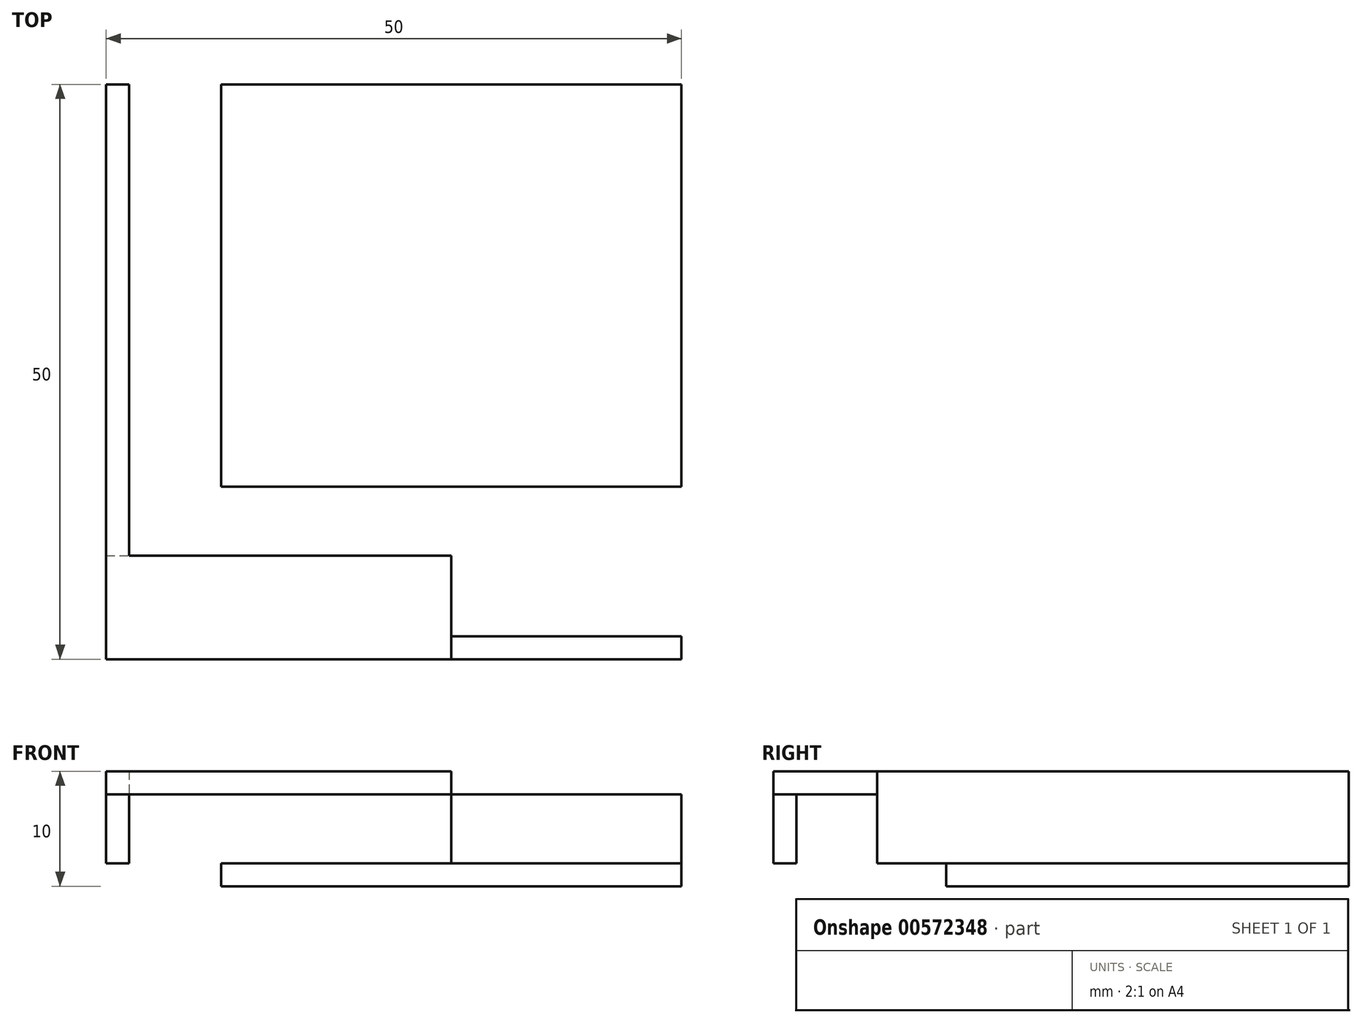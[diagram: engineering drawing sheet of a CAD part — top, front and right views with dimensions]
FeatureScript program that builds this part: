
annotation { "Feature Type Name" : "Feature", "Feature Type Description" : "" }
export const myFeature = defineFeature(function(context is Context, id is Id, definition is map)
    precondition{}
    {
        {
            var Q0;
            Q0=qCreatedBy(makeId("Top.planeOp"),FACE);
            var sketch = newSketch(context, id + "F0", { "sketchPlane" : qUnion([Q0])});
            skLineSegment(sketch, "E0.bottom", {"start": v(-25, 25) * mm, "end": v(25, 25) * mm});
            skLineSegment(sketch, "E0.top", {"start": v(-25, -25) * mm, "end": v(25, -25) * mm});
            skLineSegment(sketch, "E0.left", {"start": v(-25, 25) * mm, "end": v(-25, -25) * mm});
            skLineSegment(sketch, "E0.right", {"start": v(25, 25) * mm, "end": v(25, -25) * mm});
            skPoint(sketch, "E0.middle", {"position": v(0, 0) * mm});
            skLineSegment(sketch, "E1.bottom", {"start": v(-25, -25) * mm, "end": v(5, -25) * mm});
            skLineSegment(sketch, "E1.top", {"start": v(-25, -16) * mm, "end": v(5, -16) * mm});
            skLineSegment(sketch, "E1.left", {"start": v(-25, -25) * mm, "end": v(-25, -16) * mm});
            skLineSegment(sketch, "E1.right", {"start": v(5, -25) * mm, "end": v(5, -16) * mm});
            skLineSegment(sketch, "E2.bottom", {"start": v(25, 25) * mm, "end": v(-15, 25) * mm});
            skLineSegment(sketch, "E2.top", {"start": v(25, -10) * mm, "end": v(-15, -10) * mm});
            skLineSegment(sketch, "E2.left", {"start": v(25, 25) * mm, "end": v(25, -10) * mm});
            skLineSegment(sketch, "E2.right", {"start": v(-15, 25) * mm, "end": v(-15, -10) * mm});
            skSolve(sketch);
        }
        {
            var Q0;
            Q0=makeQuery(id+"F0.imprint","IMPRINT",FACE,{"disambiguationData":[TD([[makeQuery(id+"F0.imprint","IMPRINT",EDGE,{"derivedFrom":sQuery(id+"F0.wireOp",EDGE,"E0.bottom")}),-1.0]])]});
            extrude(context, id + "F1", {"entities" : qUnion([Q0]), "depth" : 2 * mm, "offsetDistance" : 25 * mm});
        }
        {
            var Q0;
            Q0=makeQuery(id+"F1.opExtrude","CAP_FACE",FACE,{"disambiguationData":[OSD([sQuery(id+"F0.wireOp",EDGE,"E0.bottom"),sQuery(id+"F0.wireOp",EDGE,"E0.top"),sQuery(id+"F0.wireOp",EDGE,"E0.left"),sQuery(id+"F0.wireOp",EDGE,"E0.right"),sQuery(id+"F0.wireOp",EDGE,"E1.top"),sQuery(id+"F0.wireOp",EDGE,"E1.right")])],"isStart":false});
            var sketch = newSketch(context, id + "F2", { "sketchPlane" : qUnion([Q0])});
            skLineSegment(sketch, "E3.bottom", {"start": v(5, -25) * mm, "end": v(25, -25) * mm});
            skLineSegment(sketch, "E3.top", {"start": v(5, -23) * mm, "end": v(25, -23) * mm});
            skLineSegment(sketch, "E3.left", {"start": v(5, -25) * mm, "end": v(5, -23) * mm});
            skLineSegment(sketch, "E3.right", {"start": v(25, -25) * mm, "end": v(25, -23) * mm});
            skLineSegment(sketch, "E4.bottom", {"start": v(-25, 25) * mm, "end": v(-23, 25) * mm});
            skLineSegment(sketch, "E4.top", {"start": v(-25, -16) * mm, "end": v(-23, -16) * mm});
            skLineSegment(sketch, "E4.left", {"start": v(-25, 25) * mm, "end": v(-25, -16) * mm});
            skLineSegment(sketch, "E4.right", {"start": v(-23, 25) * mm, "end": v(-23, -16) * mm});
            skSolve(sketch);
        }
        {
            var Q0;
            Q0 = qSketchRegion(id + "F2", true);
            extrude(context, id + "F3", {"entities" : qUnion([Q0]), "operationType" : NewBodyOperationType.ADD, "depth" : 6 * mm, "offsetDistance" : 25 * mm});
        }
        {
            var Q0;
            Q0=makeQuery(id+"F3.opExtrude","CAP_FACE",FACE,{"disambiguationData":[OSD([sQuery(id+"F2.wireOp",EDGE,"E4.bottom"),sQuery(id+"F2.wireOp",EDGE,"E4.top"),sQuery(id+"F2.wireOp",EDGE,"E4.left"),sQuery(id+"F2.wireOp",EDGE,"E4.right")])],"isStart":false});
            var sketch = newSketch(context, id + "F4", { "sketchPlane" : qUnion([Q0])});
            skLineSegment(sketch, "E5.bottom", {"start": v(-25, 25) * mm, "end": v(25, 25) * mm});
            skLineSegment(sketch, "E5.top", {"start": v(-25, -25) * mm, "end": v(25, -25) * mm});
            skLineSegment(sketch, "E5.left", {"start": v(-25, 25) * mm, "end": v(-25, -25) * mm});
            skLineSegment(sketch, "E5.right", {"start": v(25, 25) * mm, "end": v(25, -25) * mm});
            skLineSegment(sketch, "E6.bottom", {"start": v(5, -25) * mm, "end": v(-25, -25) * mm});
            skLineSegment(sketch, "E6.top", {"start": v(5, -16) * mm, "end": v(-25, -16) * mm});
            skLineSegment(sketch, "E6.left", {"start": v(5, -25) * mm, "end": v(5, -16) * mm});
            skLineSegment(sketch, "E6.right", {"start": v(-25, -25) * mm, "end": v(-25, -16) * mm});
            skLineSegment(sketch, "E7.bottom", {"start": v(25, 6.5) * mm, "end": v(-13, 6.5) * mm});
            skLineSegment(sketch, "E7.top", {"start": v(25, -3.5) * mm, "end": v(-13, -3.5) * mm});
            skLineSegment(sketch, "E7.left", {"start": v(25, 6.5) * mm, "end": v(25, -3.5) * mm});
            skLineSegment(sketch, "E7.right", {"start": v(-13, 6.5) * mm, "end": v(-13, -3.5) * mm});
            skCircle(sketch, "E8", {"center": v(-13, 1.5) * mm, "radius": 7.5 * mm});
            skSolve(sketch);
        }
        {
            var Q0;
            {var subQ0=sQuery(id+"F4.wireOp",EDGE,"E5.left");Q0=makeQuery(id+"F4.imprint","IMPRINT",FACE,{"disambiguationData":[TD([[makeQuery(id+"F4.imprint","IMPRINT",EDGE,{"derivedFrom":subQ0}),1.0]])]});}
            var Q1;
            Q1=makeQuery(id+"F4.imprint","IMPRINT",FACE,{"disambiguationData":[TD([[makeQuery(id+"F4.imprint","IMPRINT",EDGE,{"derivedFrom":sQuery(id+"F4.wireOp",EDGE,"E5.top")}),1.0]])]});
            extrude(context, id + "F5", {"entities" : qUnion([Q0, Q1]), "operationType" : NewBodyOperationType.ADD, "depth" : 2 * mm, "offsetDistance" : 25 * mm});
        }
    });
